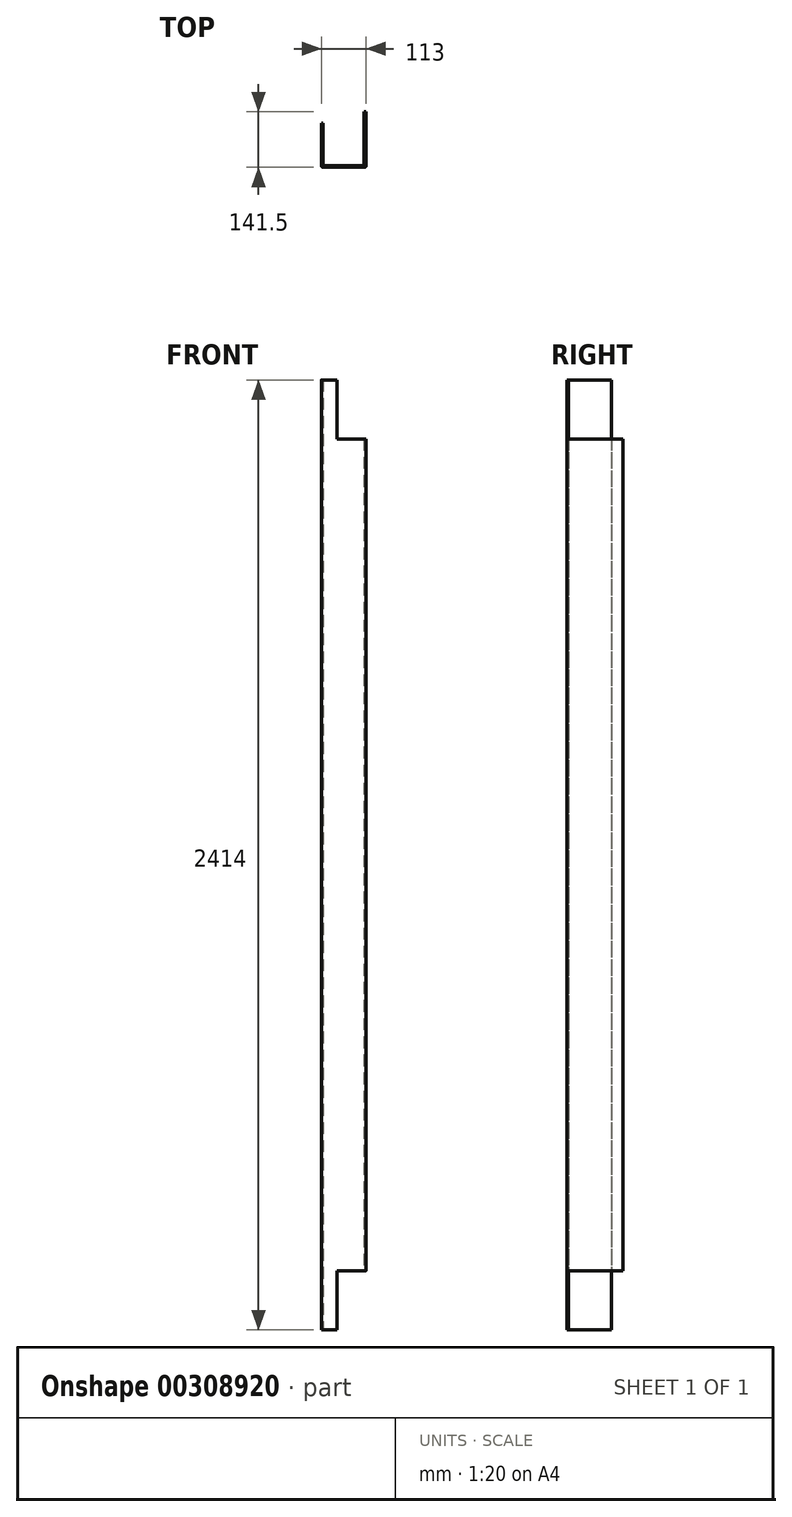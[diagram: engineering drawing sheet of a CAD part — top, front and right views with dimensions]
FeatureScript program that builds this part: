
annotation { "Feature Type Name" : "Feature", "Feature Type Description" : "" }
export const myFeature = defineFeature(function(context is Context, id is Id, definition is map)
    precondition{}
    {
        {
            var Q0;
            Q0=qCreatedBy(makeId("Top.planeOp"),FACE);
            var sketch = newSketch(context, id + "F0", { "sketchPlane" : qUnion([Q0])});
            skLineSegment(sketch, "E0", {"start": v(-59.22, 112.5) * mm, "end": v(-59.22, 4) * mm});
            skLineSegment(sketch, "E1", {"start": v(-55.22, 0) * mm, "end": v(49.78, 0) * mm});
            skLineSegment(sketch, "E2.0", {"start": v(-51.22, 4) * mm, "end": v(44.78, 4) * mm});
            skLineSegment(sketch, "E3", {"start": v(53.78, 4) * mm, "end": v(53.78, 141.5) * mm});
            skLineSegment(sketch, "E4.0", {"start": v(48.78, 8) * mm, "end": v(48.78, 141.5) * mm});
            skArc(sketch, "E5.filletArc", {"start": v(44.78, 4) * mm, "mid": v(47.6, 5.17) * mm, "end": v(48.78, 8) * mm});
            skPoint(sketch, "E6.visualSharp", {"position": v(53.78, 0) * mm});
            skArc(sketch, "E6.filletArc", {"start": v(49.78, 0) * mm, "mid": v(52.6, 1.17) * mm, "end": v(53.78, 4) * mm});
            skPoint(sketch, "E7.visualSharp", {"position": v(-55.22, 4) * mm});
            skArc(sketch, "E7.filletArc", {"start": v(-55.22, 8) * mm, "mid": v(-54.05, 5.17) * mm, "end": v(-51.22, 4) * mm});
            skPoint(sketch, "E8.visualSharp", {"position": v(-59.22, 0) * mm});
            skArc(sketch, "E8.filletArc", {"start": v(-59.22, 4) * mm, "mid": v(-58.05, 1.17) * mm, "end": v(-55.22, 0) * mm});
            skLineSegment(sketch, "E9", {"start": v(48.78, 141.5) * mm, "end": v(53.78, 141.5) * mm});
            skLineSegment(sketch, "E10", {"start": v(-59.22, 112.5) * mm, "end": v(-55.22, 112.5) * mm});
            skLineSegment(sketch, "E11", {"start": v(-55.22, 8) * mm, "end": v(-55.22, 112.5) * mm});
            skSolve(sketch);
        }
        {
            var Q0;
            Q0 = qSketchRegion(id + "F0", true);
            extrude(context, id + "F1", {"entities" : qUnion([Q0]), "depth" : 2414 * mm});
        }
        {
            var Q0;
            Q0=makeQuery(id+"F1.opExtrude","SWEPT_FACE",FACE,{"disambiguationData":[OSD([sQuery(id+"F0.wireOp",EDGE,"E1")])]});
            var sketch = newSketch(context, id + "F2", { "sketchPlane" : qUnion([Q0])});
            skLineSegment(sketch, "E12.bottom", {"start": v(145.96, 2414) * mm, "end": v(-20.22, 2414) * mm});
            skLineSegment(sketch, "E12.top", {"start": v(145.96, 2264) * mm, "end": v(-20.22, 2264) * mm});
            skLineSegment(sketch, "E12.left", {"start": v(145.96, 2414) * mm, "end": v(145.96, 2264) * mm});
            skLineSegment(sketch, "E12.right", {"start": v(-20.22, 2414) * mm, "end": v(-20.22, 2264) * mm});
            skLineSegment(sketch, "E13.0", {"start": v(-59.22, 2414) * mm, "end": v(-59.22, 0) * mm});
            skLineSegment(sketch, "E14.0", {"start": v(53.78, 2414) * mm, "end": v(53.78, 0) * mm});
            skLineSegment(sketch, "E15", {"start": v(49.78, 1207) * mm, "end": v(553.52, 1207) * mm});
            skPoint(sketch, "E15.endSnap0", {"position": v(49.78, 1207) * mm});
            skLineSegment(sketch, "E16.MirrorCS", {"start": v(-20.22, 0) * mm, "end": v(-20.22, 150) * mm});
            skLineSegment(sketch, "E17.MirrorCS", {"start": v(145.96, 0) * mm, "end": v(145.96, 150) * mm});
            skLineSegment(sketch, "E18.MirrorCS", {"start": v(145.96, 150) * mm, "end": v(-20.22, 150) * mm});
            skLineSegment(sketch, "E19.MirrorCS", {"start": v(145.96, 0) * mm, "end": v(-20.22, 0) * mm});
            skSolve(sketch);
        }
        {
            var Q0;
            {var subQ0=sQuery(id+"F2.wireOp",EDGE,"E12.left");Q0=makeQuery(id+"F2.imprint","IMPRINT",FACE,{"disambiguationData":[TD([[makeQuery(id+"F2.imprint","IMPRINT",EDGE,{"derivedFrom":subQ0}),-1.0]])]});}
            var Q1;
            {var subQ4=sQuery(id+"F2.wireOp",EDGE,"E12.right");Q1=makeQuery(id+"F2.imprint","IMPRINT",FACE,{"disambiguationData":[TD([[makeQuery(id+"F2.imprint","IMPRINT",EDGE,{"derivedFrom":subQ4}),1.0]])]});}
            var Q2;
            {var subQ0=sQuery(id+"F2.wireOp",EDGE,"E12.bottom");var subQ3=sQuery(id+"F2.wireOp",EDGE,"E14.0");var subQ4=makeQuery(id+"F2.imprint","INTERSECT",VERTEX,{"derivedFrom":[subQ0,subQ3]});Q2=makeQuery(id+"F2.imprint","IMPRINT",FACE,{"disambiguationData":[TD([[makeQuery(id+"F2.imprint","IMPRINT",EDGE,{"disambiguationData":[TD([[subQ4,-1.0]])],"derivedFrom":subQ3}),-1.0]])]});}
            var Q3;
            {var subQ0=sQuery(id+"F2.wireOp",EDGE,"E19.MirrorCS");var subQ1=sQuery(id+"F2.wireOp",EDGE,"E14.0");var subQ2=makeQuery(id+"F2.imprint","INTERSECT",VERTEX,{"derivedFrom":[subQ1,subQ0]});Q3=makeQuery(id+"F2.imprint","IMPRINT",FACE,{"disambiguationData":[TD([[makeQuery(id+"F2.imprint","IMPRINT",EDGE,{"disambiguationData":[TD([[subQ2,1.0]])],"derivedFrom":subQ1}),-1.0]])]});}
            var Q4;
            {var subQ5=sQuery(id+"F2.wireOp",EDGE,"E17.MirrorCS");Q4=makeQuery(id+"F2.imprint","IMPRINT",FACE,{"disambiguationData":[TD([[makeQuery(id+"F2.imprint","IMPRINT",EDGE,{"derivedFrom":subQ5}),1.0]])]});}
            var Q5;
            {var subQ0=sQuery(id+"F2.wireOp",EDGE,"E16.MirrorCS");Q5=makeQuery(id+"F2.imprint","IMPRINT",FACE,{"disambiguationData":[TD([[makeQuery(id+"F2.imprint","IMPRINT",EDGE,{"derivedFrom":subQ0}),-1.0]])]});}
            extrude(context, id + "F3", {"entities" : qUnion([Q0, Q1, Q2, Q3, Q4, Q5]), "operationType" : NewBodyOperationType.REMOVE, "endBound" : BoundingType.THROUGH_ALL, "oppositeDirection" : true, "depth" : 25 * mm});
        }
    });
